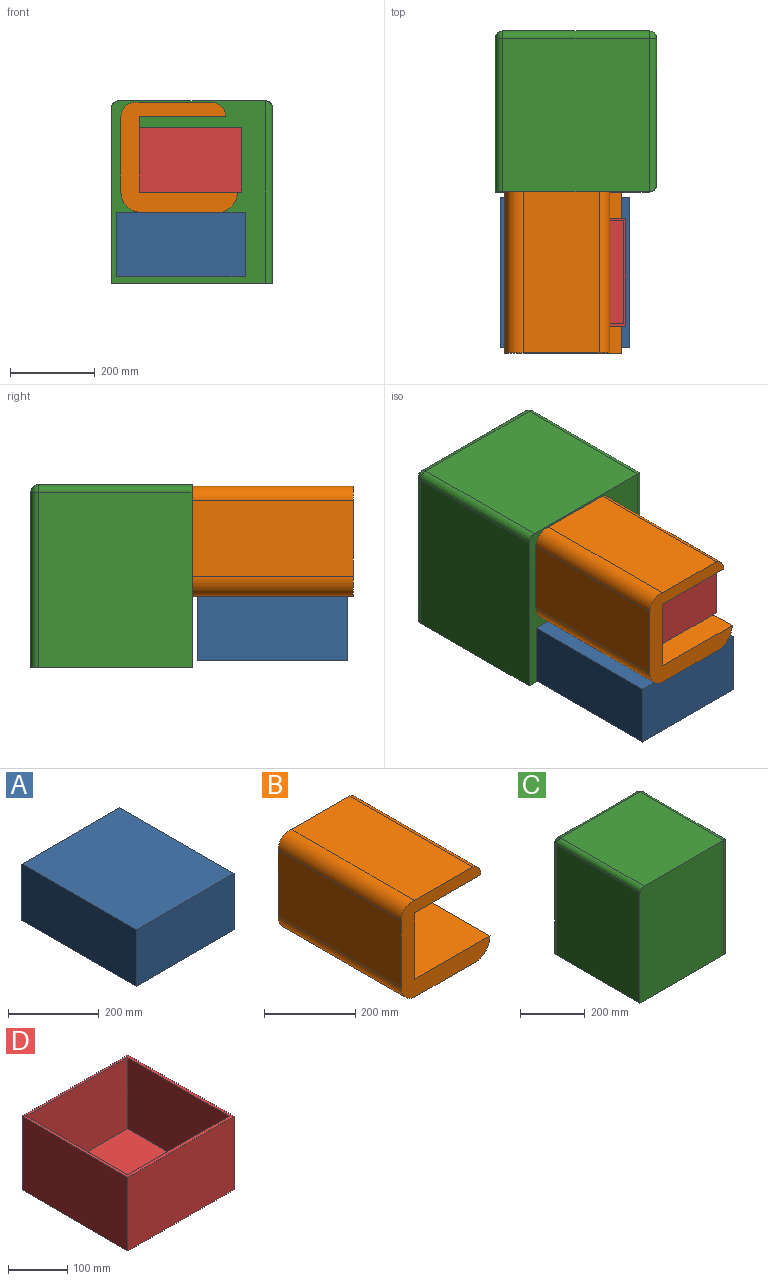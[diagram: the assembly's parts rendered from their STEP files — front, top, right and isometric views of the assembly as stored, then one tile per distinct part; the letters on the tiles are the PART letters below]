
ASSEMBLY  parts=4 mates=3
PART A: 6 faces, bbox 304.8x355.6x152.4 mm
  f0: plane 304.8x152.4mm, normal (0,1,0), area 46451.5mm2, adj f1,f3,f4,f5
  f1: plane 355.6x152.4mm, normal (-1,0,0), area 54193.4mm2, adj f0,f2,f4,f5
  f2: plane 304.8x152.4mm, normal (0,-1,0), area 46451.5mm2, adj f1,f3,f4,f5
  f3: plane 355.6x152.4mm, normal (1,0,0), area 54193.4mm2, adj f0,f2,f4,f5
  f4: plane 355.6x304.8mm, normal (0,0,1), area 108386.9mm2, adj f0,f1,f2,f3
  f5: plane 355.6x304.8mm, normal (0,0,-1), area 108386.9mm2, adj f0,f1,f2,f3
PART B: 12 faces, bbox 275.6x381x260 mm
  f0: plane 381x177.8mm, normal (-1,0,0), area 67741.8mm2, adj f1,f9,f10,f11
  f1: cylinder r=47.94mm len=381mm, axis (0,1,0), area 26716.5mm2, adj f0,f2,f10,f11
  f2: plane 381x196.74mm, normal (0,0,-1), area 74958.3mm2, adj f1,f3,f10,f11
  f3: cylinder r=49.53mm len=381mm, axis (0,1,0), area 24439.8mm2, adj f2,f4,f10,f11
  f4: plane 381x232.79mm, normal (0,0,1), area 88692.9mm2, adj f3,f5,f10,f11
  f5: plane 381x177.8mm, normal (1,0,0), area 67741.8mm2, adj f4,f6,f10,f11
  f6: plane 381x204.68mm, normal (0,0,-1), area 77984.5mm2, adj f5,f7,f10,f11
  f7: cylinder r=35.07mm len=381mm, axis (0,1,0), area 17116.3mm2, adj f6,f8,f10,f11
  f8: plane 381x179.63mm, normal (0,0,1), area 68440.2mm2, adj f7,f9,f10,f11
  f9: cylinder r=34.59mm len=381mm, axis (0,1,0), area 23846.8mm2, adj f0,f8,f10,f11
  f10: plane 275.56x260.04mm, normal (0,-1,0), area 27681.4mm2, adj f0,f1,f2,f3,f4,f5,f6,f7
  f11: plane 275.56x260.04mm, normal (0,1,0), area 27681.4mm2, adj f0,f1,f2,f3,f4,f5,f6,f7
PART C: 14 faces, bbox 381x381x431.8 mm
  f0: plane 414.02x363.22mm, normal (-1,0,0), area 150380.3mm2, adj f1,f5,f6,f7
  f1: plane 431.8x363.22mm, normal (0,-1,0), area 156770.6mm2, adj f0,f4,f5,f6,f13
  f2: plane 414.02x345.44mm, normal (1,0,0), area 143019.1mm2, adj f5,f10,f12,f13
  f3: plane 414.02x345.44mm, normal (0,1,0), area 143019.1mm2, adj f5,f7,f9,f10
  f4: plane 363.22x345.44mm, normal (0,0,1), area 125470.7mm2, adj f1,f6,f9,f12
  f5: plane 381x381mm, normal (0,0,-1), area 144957.5mm2, adj f0,f1,f2,f3,f7,f10,f13
  f6: cylinder r=17.78mm len=363.22mm, axis (0,1,0), area 10144.3mm2, adj f0,f1,f4,f8
  f7: cylinder r=17.78mm len=414.02mm, axis (0,0,-1), area 11563.1mm2, adj f0,f3,f5,f8
  f8: sphere r=17.78mm, area 496.6mm2, adj f6,f7,f9
  f9: cylinder r=17.78mm len=345.44mm, axis (1,0,0), area 9647.7mm2, adj f3,f4,f8,f11
  f10: cylinder r=17.78mm len=414.02mm, axis (0,0,1), area 11563.1mm2, adj f2,f3,f5,f11
  f11: sphere r=17.78mm, area 496.6mm2, adj f9,f10,f12
  f12: cylinder r=17.78mm len=363.22mm, axis (0,-1,0), area 9963.8mm2, adj f2,f4,f11,f13
  f13: cylinder r=17.78mm len=431.8mm, axis (0,0,-1), area 11879.2mm2, adj f1,f2,f5,f12
PART D: 11 faces, bbox 254x254x152.4 mm
  f0: plane 254x254mm, normal (0,0,1), area 5304mm2, adj f1,f3,f4,f5,f6,f7,f8,f9
  f1: plane 254x152.4mm, normal (-1,0,0), area 38709.6mm2, adj f0,f2,f4,f5
  f2: plane 254x254mm, normal (0,0,-1), area 64516mm2, adj f1,f3,f4,f5
  f3: plane 254x152.4mm, normal (1,0,0), area 38709.6mm2, adj f0,f2,f4,f5
  f4: plane 254x152.4mm, normal (0,-1,0), area 38709.6mm2, adj f0,f1,f2,f3
  f5: plane 254x152.4mm, normal (0,1,0), area 38709.6mm2, adj f0,f1,f2,f3
  f6: plane 243.3x147.32mm, normal (0,-1,0), area 35843.1mm2, adj f0,f7,f9,f10
  f7: plane 243.37x147.32mm, normal (1,0,0), area 35853.2mm2, adj f0,f6,f8,f10
  f8: plane 243.3x147.32mm, normal (0,1,0), area 35843.1mm2, adj f0,f7,f9,f10
  f9: plane 243.37x147.32mm, normal (-1,0,0), area 35853.2mm2, adj f0,f6,f8,f10
  f10: plane 243.37x243.3mm, normal (0,0,1), area 59212mm2, adj f6,f7,f8,f9
PLACE A t=(80.37,-246.75,7.87)mm
PLACE B t=(122.51,29.37,263.15)mm
PLACE C t=(-40.96,29.37,-7.88)mm
PLACE D t=(157.74,-34.13,313.44)mm
MATE fastened A.f4 <-> B.f2  axis (0,0,1) through (122.7,-161.13,160.27)mm
MATE fastened D.f2 <-> B.f4  axis (0,0,-1) through (140.72,-161.13,207.93)mm
MATE fastened B.f11 <-> C.f1  axis (0,1,0) through (140.72,29.37,207.93)mm
